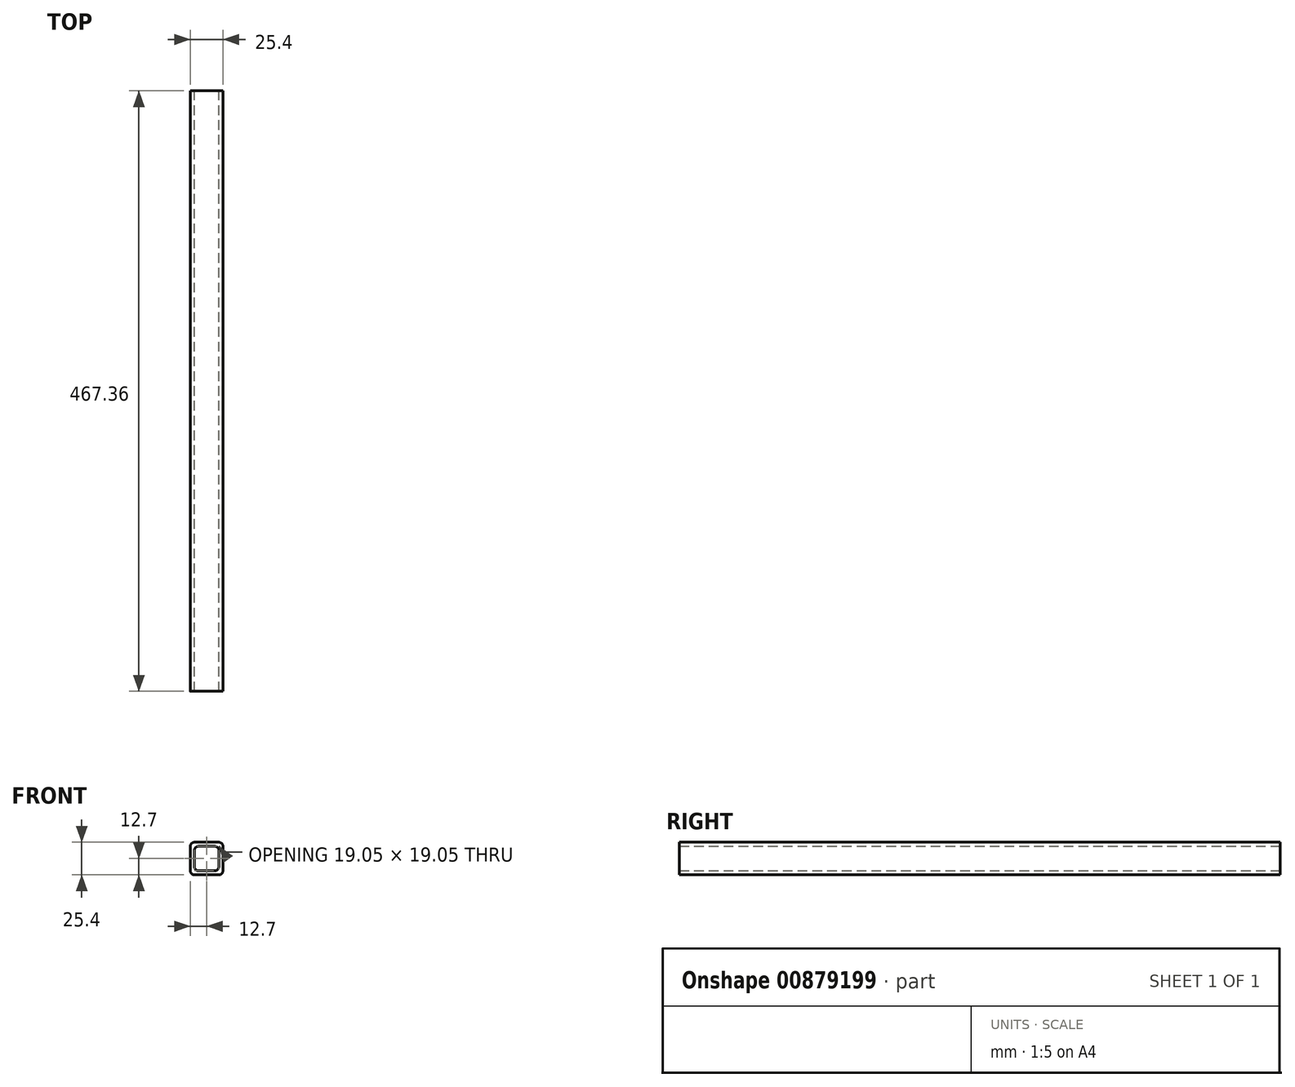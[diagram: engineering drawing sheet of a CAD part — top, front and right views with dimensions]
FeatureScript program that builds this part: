
annotation { "Feature Type Name" : "Feature", "Feature Type Description" : "" }
export const myFeature = defineFeature(function(context is Context, id is Id, definition is map)
    precondition{}
    {
        {
            var Q0;
            Q0=qCreatedBy(makeId("Front.planeOp"),FACE);
            var sketch = newSketch(context, id + "F0", { "sketchPlane" : qUnion([Q0])});
            skLineSegment(sketch, "E0.bottom", {"start": v(9.53, -12.7) * mm, "end": v(-9.52, -12.7) * mm});
            skLineSegment(sketch, "E0.top", {"start": v(9.53, 12.7) * mm, "end": v(-9.53, 12.7) * mm});
            skLineSegment(sketch, "E0.left", {"start": v(12.7, -9.53) * mm, "end": v(12.7, 9.53) * mm});
            skLineSegment(sketch, "E0.right", {"start": v(-12.7, -9.53) * mm, "end": v(-12.7, 9.52) * mm});
            skLineSegment(sketch, "E1.bottom", {"start": v(6.35, -9.52) * mm, "end": v(-6.35, -9.53) * mm});
            skLineSegment(sketch, "E1.top", {"start": v(6.35, 9.53) * mm, "end": v(-6.35, 9.52) * mm});
            skLineSegment(sketch, "E1.left", {"start": v(9.52, -6.35) * mm, "end": v(9.52, 6.35) * mm});
            skLineSegment(sketch, "E1.right", {"start": v(-9.52, -6.35) * mm, "end": v(-9.53, 6.35) * mm});
            skPoint(sketch, "E2.visualSharp", {"position": v(9.52, 9.53) * mm});
            skArc(sketch, "E2.filletArc", {"start": v(9.53, 6.35) * mm, "mid": v(8.6, 8.6) * mm, "end": v(6.35, 9.53) * mm});
            skPoint(sketch, "E3.visualSharp", {"position": v(-9.53, 9.53) * mm});
            skArc(sketch, "E3.filletArc", {"start": v(-6.35, 9.53) * mm, "mid": v(-8.6, 8.6) * mm, "end": v(-9.53, 6.35) * mm});
            skPoint(sketch, "E4.visualSharp", {"position": v(-9.52, -9.53) * mm});
            skArc(sketch, "E4.filletArc", {"start": v(-9.52, -6.35) * mm, "mid": v(-8.6, -8.6) * mm, "end": v(-6.35, -9.53) * mm});
            skPoint(sketch, "E5.visualSharp", {"position": v(9.53, -9.52) * mm});
            skArc(sketch, "E5.filletArc", {"start": v(6.35, -9.52) * mm, "mid": v(8.6, -8.6) * mm, "end": v(9.52, -6.35) * mm});
            skPoint(sketch, "E6.visualSharp", {"position": v(12.7, 12.7) * mm});
            skArc(sketch, "E6.filletArc", {"start": v(12.7, 9.53) * mm, "mid": v(11.77, 11.77) * mm, "end": v(9.53, 12.7) * mm});
            skPoint(sketch, "E7.visualSharp", {"position": v(-12.7, 12.7) * mm});
            skArc(sketch, "E7.filletArc", {"start": v(-9.53, 12.7) * mm, "mid": v(-11.77, 11.77) * mm, "end": v(-12.7, 9.52) * mm});
            skPoint(sketch, "E8.visualSharp", {"position": v(-12.7, -12.7) * mm});
            skArc(sketch, "E8.filletArc", {"start": v(-12.7, -9.53) * mm, "mid": v(-11.77, -11.77) * mm, "end": v(-9.52, -12.7) * mm});
            skPoint(sketch, "E9.visualSharp", {"position": v(12.7, -12.7) * mm});
            skArc(sketch, "E9.filletArc", {"start": v(9.53, -12.7) * mm, "mid": v(11.77, -11.77) * mm, "end": v(12.7, -9.53) * mm});
            skSolve(sketch);
        }
        {
            var Q0;
            Q0=qSketchRegion(id+"F0",true);
            extrude(context, id + "F1", {"entities" : qUnion([Q0]), "depth" : 467.36 * mm, "offsetDistance" : 25.4 * mm});
        }
    });
